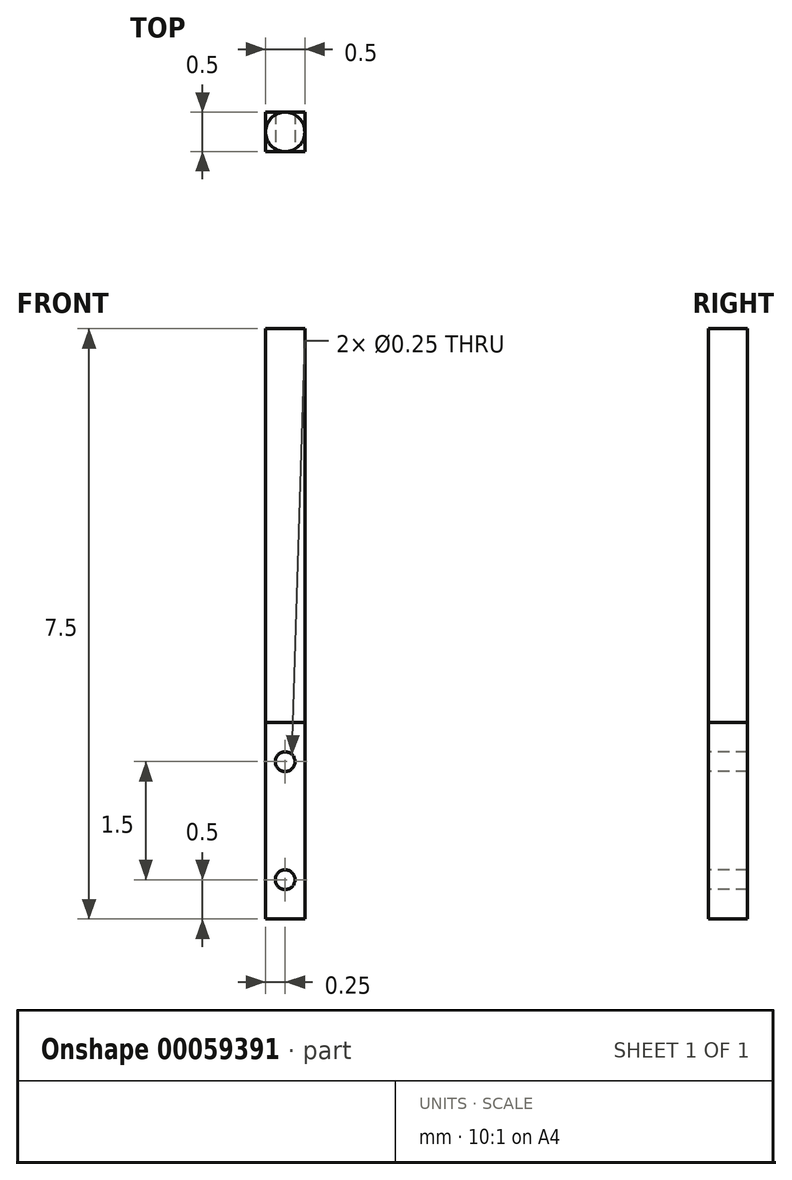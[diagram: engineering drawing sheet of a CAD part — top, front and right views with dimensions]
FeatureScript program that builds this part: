
annotation { "Feature Type Name" : "Feature", "Feature Type Description" : "" }
export const myFeature = defineFeature(function(context is Context, id is Id, definition is map)
    precondition{}
    {
        {
            var Q0;
            Q0=qCreatedBy(makeId("Top.planeOp"),FACE);
            var sketch = newSketch(context, id + "F0", { "sketchPlane" : qUnion([Q0])});
            skLineSegment(sketch, "E0.rect.bottom", {"start": v(0.25, -0.25) * mm, "end": v(-0.25, -0.25) * mm});
            skLineSegment(sketch, "E0.rect.top", {"start": v(0.25, 0.25) * mm, "end": v(-0.25, 0.25) * mm});
            skLineSegment(sketch, "E0.rect.left", {"start": v(0.25, -0.25) * mm, "end": v(0.25, 0.25) * mm});
            skLineSegment(sketch, "E0.rect.right", {"start": v(-0.25, -0.25) * mm, "end": v(-0.25, 0.25) * mm});
            skPoint(sketch, "E0.rect.middle", {"position": v(0, 0) * mm});
            skSolve(sketch);
        }
        {
            var Q0;
            Q0 = qSketchRegion(id + "F0", true);
            extrude(context, id + "F1", {"entities" : qUnion([Q0]), "depth" : 2 * mm, "hasSecondDirection" : true, "secondDirectionOppositeDirection" : true, "secondDirectionDepth" : 0.5 * mm});
        }
        {
            var Q0;
            Q0=makeQuery(id+"F1.opExtrude","CAP_FACE",FACE,{"disambiguationData":[OSD([sQuery(id+"F0.wireOp",EDGE,"E0.rect.bottom"),sQuery(id+"F0.wireOp",EDGE,"E0.rect.top"),sQuery(id+"F0.wireOp",EDGE,"E0.rect.left"),sQuery(id+"F0.wireOp",EDGE,"E0.rect.right")])],"isStart":false});
            var sketch = newSketch(context, id + "F2", { "sketchPlane" : qUnion([Q0])});
            skCircle(sketch, "E1", {"center": v(0, 0) * mm, "radius": 0.25 * mm});
            skSolve(sketch);
        }
        {
            var Q0;
            {var subQ0=sQuery(id+"F2.wireOp",EDGE,"E1");var subQ1=makeQuery(id+"F2.imprint","INTERSECT",VERTEX,{"derivedFrom":[makeQuery(id+"F1.opExtrude","CAP_EDGE",EDGE,{"disambiguationData":[OSD([sQuery(id+"F0.wireOp",EDGE,"E0.rect.top")])],"isStart":false}),subQ0]});Q0=makeQuery(id+"F2.imprint","IMPRINT",FACE,{"disambiguationData":[TD([[makeQuery(id+"F2.imprint","IMPRINT",EDGE,{"disambiguationData":[TD([[subQ1,1.0]])],"derivedFrom":subQ0}),1.0]])]});}
            extrude(context, id + "F3", {"entities" : qUnion([Q0]), "operationType" : NewBodyOperationType.ADD, "depth" : 5 * mm});
        }
        {
            var Q0;
            Q0=qCreatedBy(makeId("Front.planeOp"),FACE);
            var sketch = newSketch(context, id + "F4", { "sketchPlane" : qUnion([Q0])});
            skCircle(sketch, "E2", {"center": v(0, 0) * mm, "radius": 0.12 * mm});
            skCircle(sketch, "E3", {"center": v(0, 1.5) * mm, "radius": 0.12 * mm});
            skSolve(sketch);
        }
        {
            var Q0;
            Q0 = qSketchRegion(id + "F4", true);
            extrude(context, id + "F5", {"entities" : qUnion([Q0]), "operationType" : NewBodyOperationType.REMOVE, "endBound" : BoundingType.SYMMETRIC, "oppositeDirection" : true, "depth" : 25 * mm});
        }
    });
